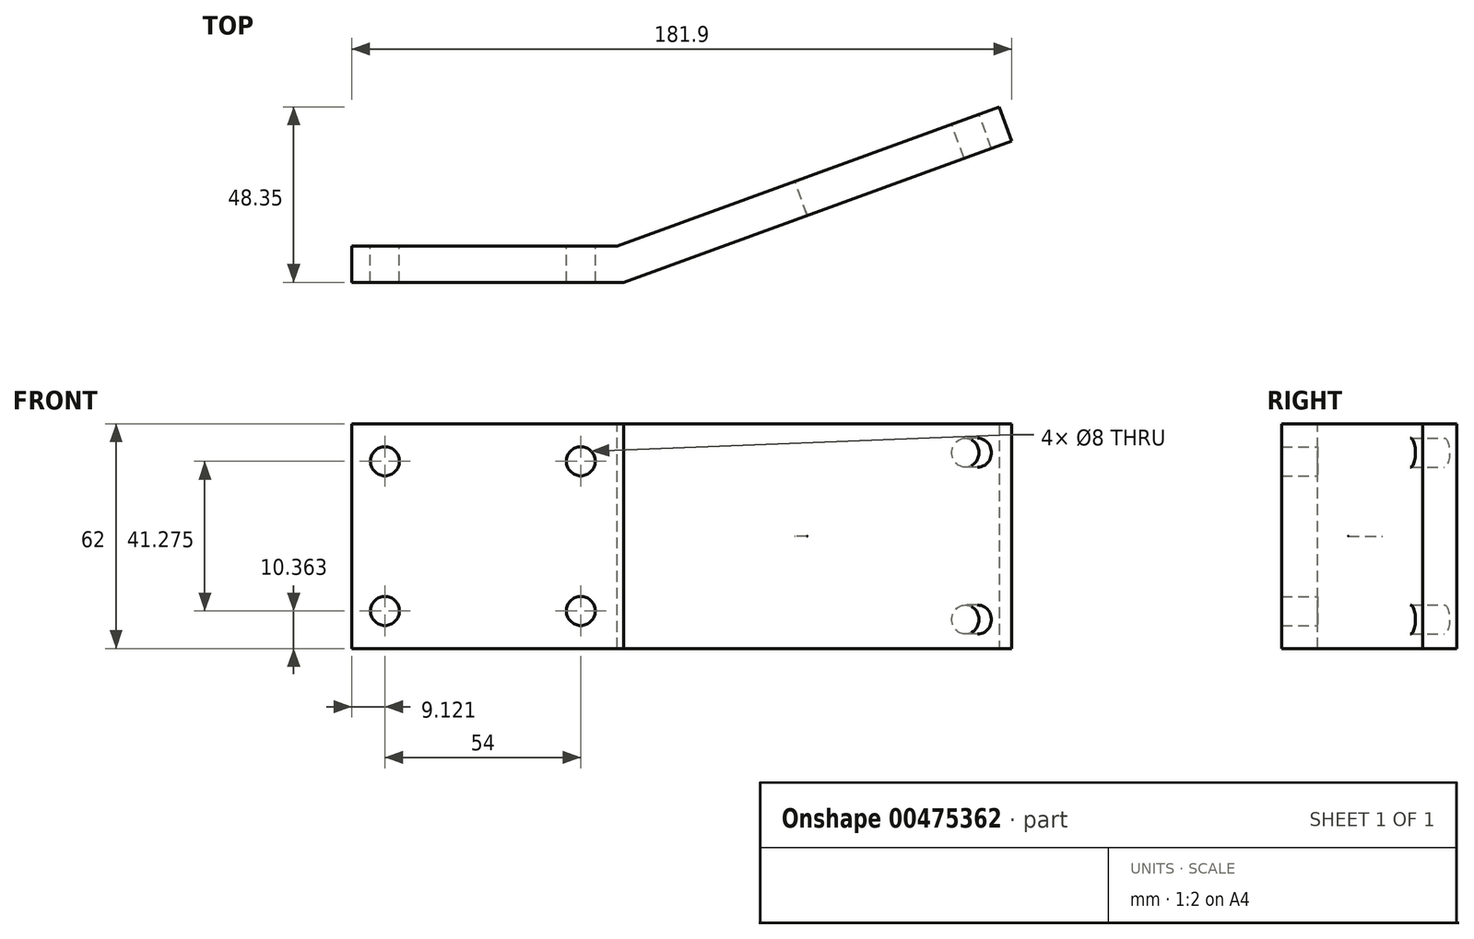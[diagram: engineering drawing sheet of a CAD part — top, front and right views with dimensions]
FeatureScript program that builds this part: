
annotation { "Feature Type Name" : "Feature", "Feature Type Description" : "" }
export const myFeature = defineFeature(function(context is Context, id is Id, definition is map)
    precondition{}
    {
        {
            var Q0;
            Q0=qCreatedBy(makeId("Top.planeOp"),FACE);
            var sketch = newSketch(context, id + "F0", { "sketchPlane" : qUnion([Q0])});
            skLineSegment(sketch, "E0", {"start": v(0, 0) * mm, "end": v(-113, 0) * mm});
            skLineSegment(sketch, "E1", {"start": v(-113, 0) * mm, "end": v(-182.54, 25.3) * mm});
            skLineSegment(sketch, "E2", {"start": v(-113, 0) * mm, "end": v(-14.61, -35.8) * mm});
            skSolve(sketch);
        }
        {
            var Q0;
            Q0=qCreatedBy(makeId("Right.planeOp"),FACE);
            var sketch = newSketch(context, id + "F1", { "sketchPlane" : qUnion([Q0])});
            skLineSegment(sketch, "E3.bottom", {"start": v(5, 31) * mm, "end": v(-5, 31) * mm});
            skLineSegment(sketch, "E3.top", {"start": v(5, -31) * mm, "end": v(-5, -31) * mm});
            skLineSegment(sketch, "E3.left", {"start": v(5, 31) * mm, "end": v(5, -31) * mm});
            skLineSegment(sketch, "E3.right", {"start": v(-5, 31) * mm, "end": v(-5, -31) * mm});
            skPoint(sketch, "E3.middle", {"position": v(0, 0) * mm});
            skSolve(sketch);
        }
        {
            var Q0;
            Q0=makeQuery(id+"F1.imprint","IMPRINT",FACE,{"disambiguationData":[TD([[makeQuery(id+"F1.imprint","IMPRINT",EDGE,{"derivedFrom":sQuery(id+"F1.wireOp",EDGE,"E3.bottom")}),1.0]])]});
            var Q1;
            Q1=sQuery(id+"F0.wireOp",EDGE,"E0");
            var Q2;
            Q2=sQuery(id+"F0.wireOp",EDGE,"E1");
            sweep(context, id + "F2", {"profiles" : qUnion([Q0]), "path" : qUnion([Q1, Q2])});
        }
        {
            var Q0;
            Q0=makeQuery(id+"F2.opSweep","SWEPT_FACE",FACE,{"disambiguationData":[OSD([sQuery(id+"F0.wireOp",EDGE,"E0"),sQuery(id+"F1.wireOp",EDGE,"E3.left")])]});
            var sketch = newSketch(context, id + "F3", { "sketchPlane" : qUnion([Q0])});
            skPoint(sketch, "E4", {"position": v(0, 0) * mm});
            skPoint(sketch, "E5", {"position": v(60, 0) * mm});
            skPoint(sketch, "E6", {"position": v(10, -23) * mm});
            skPoint(sketch, "E7", {"position": v(52, -23) * mm});
            skPoint(sketch, "E8", {"position": v(10, 23) * mm});
            skSolve(sketch);
        }
        {
            var Q0;
            Q0=sQuery(id+"F3.wireOp",VERTEX,"E6");
            var Q1;
            Q1=sQuery(id+"F3.wireOp",VERTEX,"E8");
            var Q2;
            Q2=makeQuery(id+"F2.opSweep","SWEPT_BODY",BODY,{"disambiguationData":[OSD([sQuery(id+"F0.wireOp",EDGE,"E1"),sQuery(id+"F1.wireOp",EDGE,"E3.bottom"),sQuery(id+"F1.wireOp",EDGE,"E3.top"),sQuery(id+"F1.wireOp",EDGE,"E3.left"),sQuery(id+"F1.wireOp",EDGE,"E3.right")])]});
            hole(context, id + "F4", {"style" : HoleStyle.SIMPLE, "endStyle" : HoleEndStyle.THROUGH, "standardTappedOrClearance" : lookupTablePath({ "standard" : "ISO", "size" : "8", "type" : "Drilled" }), "standardBlindInLast" : lookupTablePath({ "standard" : "ISO", "size" : "8", "type" : "Drilled" }), "holeDiameter" : 8 * mm, "isTappedThrough" : true, "tappedDepth" : 12 * mm, "tapClearance" : 3, "locations" : qUnion([Q0, Q1]), "scope" : qUnion([Q2])});
        }
        {
            var Q0;
            Q0=sQuery(id+"F3.wireOp",VERTEX,"E5");
            var Q1;
            Q1=makeQuery(id+"F2.opSweep","SWEPT_BODY",BODY,{"disambiguationData":[OSD([sQuery(id+"F0.wireOp",EDGE,"E1"),sQuery(id+"F1.wireOp",EDGE,"E3.bottom"),sQuery(id+"F1.wireOp",EDGE,"E3.top"),sQuery(id+"F1.wireOp",EDGE,"E3.left"),sQuery(id+"F1.wireOp",EDGE,"E3.right")])]});
            hole(context, id + "F5", {"style" : HoleStyle.SIMPLE, "endStyle" : HoleEndStyle.THROUGH, "standardTappedOrClearance" : lookupTablePath({ "standard" : "ANSI", "size" : "3/8 (0.38)", "type" : "Drilled" }), "standardBlindInLast" : lookupTablePath({ "standard" : "ANSI", "size" : "3/8", "type" : "Drilled" }), "holeDiameter" : 3 / 203.2 * mm, "isTappedThrough" : true, "tappedDepth" : 12 * mm, "tapClearance" : 3, "locations" : qUnion([Q0]), "scope" : qUnion([Q1])});
        }
        {
            var Q0;
            Q0=makeQuery(id+"F2.opSweep","SWEPT_FACE",FACE,{"disambiguationData":[OSD([sQuery(id+"F0.wireOp",EDGE,"E1"),sQuery(id+"F1.wireOp",EDGE,"E3.left")])]});
            var sketch = newSketch(context, id + "F6", { "sketchPlane" : qUnion([Q0])});
            skPoint(sketch, "E9", {"position": v(117.07, 0) * mm});
            skPoint(sketch, "E9.positionSnap0", {"position": v(107.07, 0) * mm});
            skPoint(sketch, "E10", {"position": v(117.07, 20.64) * mm});
            skPoint(sketch, "E11", {"position": v(117.07, -20.64) * mm});
            skPoint(sketch, "E12", {"position": v(171.07, -20.64) * mm});
            skPoint(sketch, "E13", {"position": v(171.07, 20.64) * mm});
            skPoint(sketch, "E14", {"position": v(144.07, 0) * mm});
            skSolve(sketch);
        }
        {
            var Q0;
            Q0=sQuery(id+"F6.wireOp",VERTEX,"E10");
            var Q1;
            Q1=sQuery(id+"F6.wireOp",VERTEX,"E13");
            var Q2;
            Q2=sQuery(id+"F6.wireOp",VERTEX,"E12");
            var Q3;
            Q3=sQuery(id+"F6.wireOp",VERTEX,"E11");
            var Q4;
            Q4=makeQuery(id+"F2.opSweep","SWEPT_BODY",BODY,{"disambiguationData":[OSD([sQuery(id+"F0.wireOp",EDGE,"E1"),sQuery(id+"F1.wireOp",EDGE,"E3.bottom"),sQuery(id+"F1.wireOp",EDGE,"E3.top"),sQuery(id+"F1.wireOp",EDGE,"E3.left"),sQuery(id+"F1.wireOp",EDGE,"E3.right")])]});
            hole(context, id + "F7", {"style" : HoleStyle.SIMPLE, "endStyle" : HoleEndStyle.THROUGH, "standardTappedOrClearance" : lookupTablePath({ "standard" : "ISO", "size" : "8", "type" : "Drilled" }), "standardBlindInLast" : lookupTablePath({ "standard" : "ISO", "size" : "8", "type" : "Drilled" }), "holeDiameter" : 8 * mm, "isTappedThrough" : true, "tappedDepth" : 12 * mm, "tapClearance" : 3, "locations" : qUnion([Q0, Q1, Q2, Q3]), "scope" : qUnion([Q4])});
        }
        {
            var Q0;
            Q0=makeQuery(id+"F2.opSweep","SWEPT_BODY",BODY,{"disambiguationData":[OSD([sQuery(id+"F0.wireOp",EDGE,"E1"),sQuery(id+"F1.wireOp",EDGE,"E3.bottom"),sQuery(id+"F1.wireOp",EDGE,"E3.top"),sQuery(id+"F1.wireOp",EDGE,"E3.left"),sQuery(id+"F1.wireOp",EDGE,"E3.right")])]});
            var Q1;
            Q1=makeQuery(id+"F2.opSweep","CAP_EDGE",EDGE,{"disambiguationData":[OSD([sQuery(id+"F0.wireOp",VERTEX,"E1.end"),sQuery(id+"F1.wireOp",EDGE,"E3.right")])],"isStart":false});
            transform(context, id + "F8", {"entities" : qUnion([Q0]), "transformType" : TransformType.ROTATION, "transformAxis" : qUnion([Q1]), "angle" : 20 * degree, "oppositeDirection" : true, "makeCopy" : false});
        }
    });
